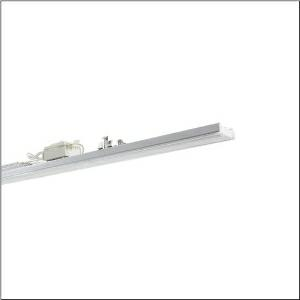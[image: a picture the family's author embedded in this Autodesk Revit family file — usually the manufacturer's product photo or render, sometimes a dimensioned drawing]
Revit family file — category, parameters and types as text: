
# Revit family: licross_r__21_recessed_mo_52tl19mn4a5g_a44e
name_source: partatom
category: Lighting Fixtures
units: mm (PartAtom-declared; Revit-internal decimal feet)

## family parameters
Cut with Voids When Loaded = No
Host = Face
Light Source = No
Part Type = Normal
Room Calculation Point = No
Round Connector Dimension = Use Diameter
Shared = No

## types (1)
- --- (1 x LED, 10530 lm, 60.5 W, 4000K)
    Apparent Load = 61 VA
    CIE Flux Codes = 55 90 98 100 100
    Color Rendering = 80
    Color Temperature = 4000K
    Default Elevation = 1800 mm
    Description = Licross® 21 Recessed MO, luminaire insert, of sheet steel, galvanised, coil coated, white, length: 1.500mm, width: 66mm, height: 67mm, LED rated luminous flux: 10.530lm, light colour: 840, control gear: ON/OFF Multilumen, with plug, 3-pole, with phase selection, mains connection: 220..240V, AC, 50/60Hz, rated input power: 61W, internal wiring halogen-free, primary light control with lens, of plastic, primary optical cover: cover, of PMMA, light emission: direct distribution, primary light characteristic: double asymmetric, protection rating (complete): IP40, insulation class (complete): insulation class I (protective earthing), certification: CE, ENEC, VDE, UKCA, protection symbol: D if used in an environment without relevant dust loads with corresponding accessories, impact resistance: IK06, permissible ambient temperature for indoor applications: -35..+40°C, corresponds to IFS (International Featured Standards) requirements for safety and quality in the food industry, reducing of maximum allowable ambient temperature of 5°C with ceiling mounting, LABS conformity tested according to VDMA 24364:2018-05, packaging unit: 1 piece
    Height = 58 mm
    Lamp = 1 x LED
    Lamp Light Flux = 10530 lm
    Lamp Power = 60.5 W
    Lamp count = 1
    Length = 1500 mm
    Luminous efficacy = 174 lm/W
    Manufacturer = Siteco
    ModVariant = No
    Model = 52TL19MN4A5G
    Mounting Place = Ceiling
    Mounting Type = Pendant
    Number of Poles = 1
    OnlyDefault = Yes
    Power Factor = 1
    Product Name = Licross® 21 Recessed MO
    Product group = luminaire insert | ceiling pendant
    ProductGroupID = 902
    Protection Class = Protection class I
    Protection Degree = IP 40
    RLX_Detail_Level = 1
    RLX_Emergency_Light_Flux = 0 lm
    RLX_Emergency_Type = 0
    RLX_Emergency_Type_DB = No
    RlxData = <blob elided: 22293 chars, md5=5068e27a>
    Socket = socket
    Standby Power = 0 W
    System Light Flux = 10530 lm
    System Power = 61 W
    Type Comments = factory setting: luminous flux: 100 % | (A | C | E) | 140 mA
    Type Image = l_1296930.jpg
    URL = http://relux.com
    VarID = @adj_130447
    Voltage = 0 V
    Weight = 0.00 kg
    Width = 66 mm

## geometry (parser evidence)
native form markers: Blend x4, Sweep x11
no freeform markers — native parametric forms only
